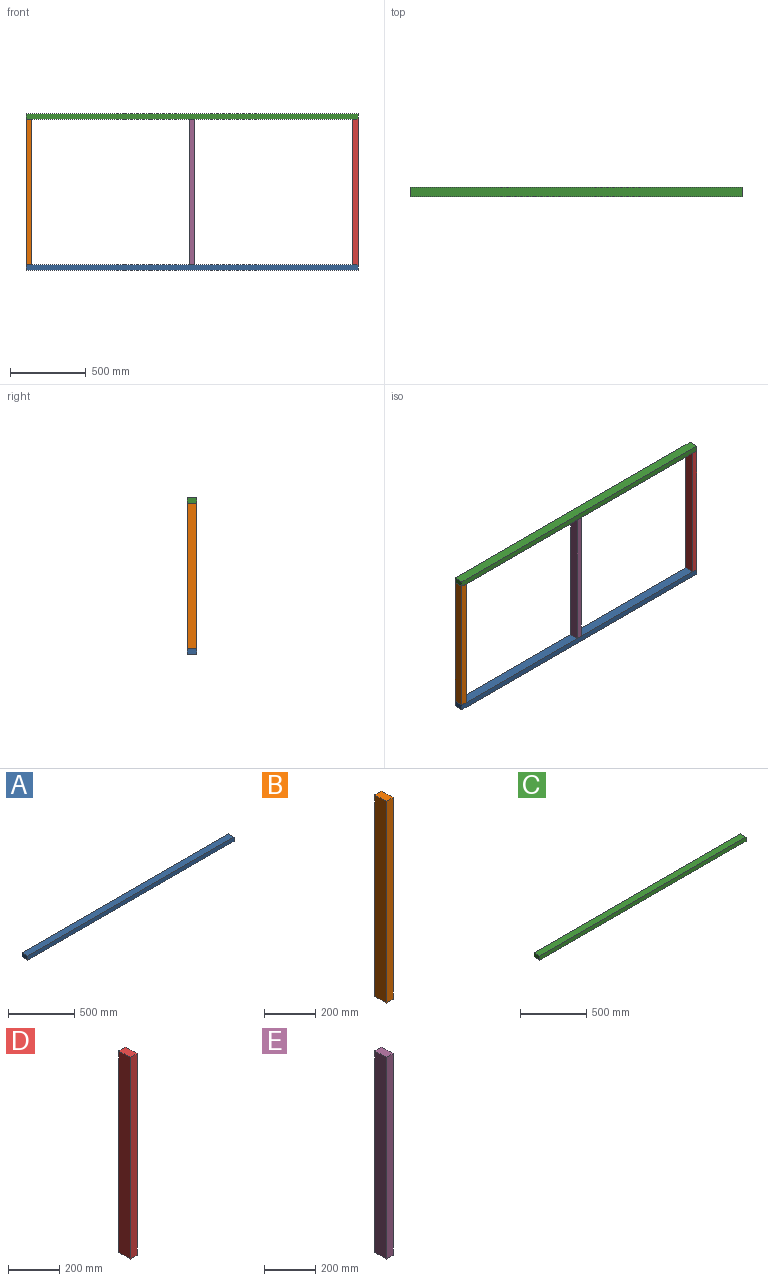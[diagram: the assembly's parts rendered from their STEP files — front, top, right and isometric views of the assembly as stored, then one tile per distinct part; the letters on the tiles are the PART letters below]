
ASSEMBLY  parts=5 mates=4
PART A: 6 faces, bbox 2195x63x38 mm
  f0: plane 63x38mm, normal (-1,0,0), area 2394mm2, adj f1,f3,f4,f5
  f1: plane 2195x38mm, normal (0,-1,0), area 83410mm2, adj f0,f2,f4,f5
  f2: plane 63x38mm, normal (1,0,0), area 2394mm2, adj f1,f3,f4,f5
  f3: plane 2195x38mm, normal (0,1,0), area 83410mm2, adj f0,f2,f4,f5
  f4: plane 2195x63mm, normal (0,0,1), area 138285mm2, adj f0,f1,f2,f3
  f5: plane 2195x63mm, normal (0,0,-1), area 138285mm2, adj f0,f1,f2,f3
PART B: 6 faces, bbox 38x63x960 mm
  f0: plane 960x38mm, normal (0,-1,0), area 36480mm2, adj f1,f3,f4,f5
  f1: plane 960x63mm, normal (1,0,0), area 60480mm2, adj f0,f2,f4,f5
  f2: plane 960x38mm, normal (0,1,0), area 36480mm2, adj f1,f3,f4,f5
  f3: plane 960x63mm, normal (-1,0,0), area 60480mm2, adj f0,f2,f4,f5
  f4: plane 63x38mm, normal (0,0,1), area 2394mm2, adj f0,f1,f2,f3
  f5: plane 63x38mm, normal (0,0,-1), area 2394mm2, adj f0,f1,f2,f3
PART C: 6 faces, bbox 2195x63x38 mm
  f0: plane 63x38mm, normal (-1,0,0), area 2394mm2, adj f1,f3,f4,f5
  f1: plane 2195x38mm, normal (0,-1,0), area 83410mm2, adj f0,f2,f4,f5
  f2: plane 63x38mm, normal (1,0,0), area 2394mm2, adj f1,f3,f4,f5
  f3: plane 2195x38mm, normal (0,1,0), area 83410mm2, adj f0,f2,f4,f5
  f4: plane 2195x63mm, normal (0,0,-1), area 138285mm2, adj f0,f1,f2,f3
  f5: plane 2195x63mm, normal (0,0,1), area 138285mm2, adj f0,f1,f2,f3
PART D: 6 faces, bbox 38x63x960 mm
  f0: plane 960x63mm, normal (-1,0,0), area 60480mm2, adj f1,f3,f4,f5
  f1: plane 960x38mm, normal (0,-1,0), area 36480mm2, adj f0,f2,f4,f5
  f2: plane 960x63mm, normal (1,0,0), area 60480mm2, adj f1,f3,f4,f5
  f3: plane 960x38mm, normal (0,1,0), area 36480mm2, adj f0,f2,f4,f5
  f4: plane 63x38mm, normal (0,0,1), area 2394mm2, adj f0,f1,f2,f3
  f5: plane 63x38mm, normal (0,0,-1), area 2394mm2, adj f0,f1,f2,f3
PART E: 6 faces, bbox 38x63x960 mm
  f0: plane 960x38mm, normal (0,1,0), area 36480mm2, adj f1,f3,f4,f5
  f1: plane 960x63mm, normal (-1,0,0), area 60480mm2, adj f0,f2,f4,f5
  f2: plane 960x38mm, normal (0,-1,0), area 36480mm2, adj f1,f3,f4,f5
  f3: plane 960x63mm, normal (1,0,0), area 60480mm2, adj f0,f2,f4,f5
  f4: plane 63x38mm, normal (0,0,1), area 2394mm2, adj f0,f1,f2,f3
  f5: plane 63x38mm, normal (0,0,-1), area 2394mm2, adj f0,f1,f2,f3
PLACE A t=(-779.07,-1294.74,-1138.67)mm
PLACE B t=(-779.07,-1294.74,-1138.67)mm
PLACE C t=(-779.07,-1294.74,-1138.67)mm
PLACE D t=(-779.07,-1294.74,-1138.67)mm
PLACE E t=(-779.07,-1294.74,-1138.67)mm
MATE fastened A.f1 <-> D.f1  axis (0,-1,0) through (1398.31,7.9,-1100.67)mm
MATE fastened A.f1 <-> E.f2  axis (0,-1,0) through (300.81,7.9,-1100.67)mm
MATE fastened D.f1 <-> C.f1  axis (0,-1,0) through (1398.31,7.9,-140.67)mm
MATE fastened A.f1 <-> B.f0  axis (0,-1,0) through (-796.69,7.9,-1100.67)mm
